# Revit family: NLRS_33_GM_FB_TC_STORAX_vloerluik_SS-50TB-EL
name_source: partatom
category: Doors
revit_build: Autodesk Revit 2015 (Build: 20140223_1515(x64)
units: mm (PartAtom-declared; Revit-internal decimal feet)

## types (1)
- RoofAccessHatchTypeSS-50TB
    Description = dakluik elektrisch bediend
    Height = 405 mm  [stored 1.32874 ft]
    IfcExportAs = IfcDoor
    IfcExportType = NOTDEFINED
    Manufacturer = Storax
    Model = SS-50TB-EL
    Rough Height = 0 mm  [stored 0 ft]
    Rough Width = 0 mm  [stored 0 ft]
    Thickness = 0 mm  [stored 0 ft]
    URL = https://www.storax.nl
    bediening = handmatig
    brandwerend 60 min = No
    breedte = 1280 mm  [stored 4.19948 ft]
    breedte_paneel = 1190 mm  [stored 3.9042 ft]
    cilinderslot = Yes
    code productgroep = LUI
    conservering = brut
    dagmaatbreedte = 1000 mm  [stored 3.28084 ft]
    dagmaatlengte = 1000 mm  [stored 3.28084 ft]
    deurblad = vlak
    false = No
    geluidsreductie (dB) = 25
    gewicht (kg) = 0
    hoogte = 405 mm  [stored 1.32874 ft]
    hoogte_aandrijving = 323 mm  [stored 1.05971 ft]
    hoogte_opstand = 305 mm  [stored 1.00066 ft]
    inhaakladder = Yes
    isolatie = Yes
    isolatiedikte = 75 mm
    isolatiewaarde = 3.5900 (m²·K)/W
    lengte_paneel = 1190 mm  [stored 3.9042 ft]
    loopslot = Yes
    materiaal = NBS_Concept
    materiaal_secundair = <By Category>
    omranding dakopstand = Yes
    omschrijving = dakluik elektrisch bediend
    openstand vergrendeling = Yes
    plaatdikte = 2 mm  [stored 0.00656168 ft]
    productgroep = Dakluiken
    scharnierend = Yes
    true = Yes
    vaste ladder = Yes
    vaste ladder met kooi = Yes
    veersysteem = Yes
    veiligheidsrailing = Yes
    waterdicht = Yes

note: [stored X ft] marks values corroborated as IEEE doubles in the binary element streams (Revit-internal decimal feet)

## geometry (parser evidence)
native form markers: Blend x8, Sweep x15
no freeform markers — native parametric forms only
